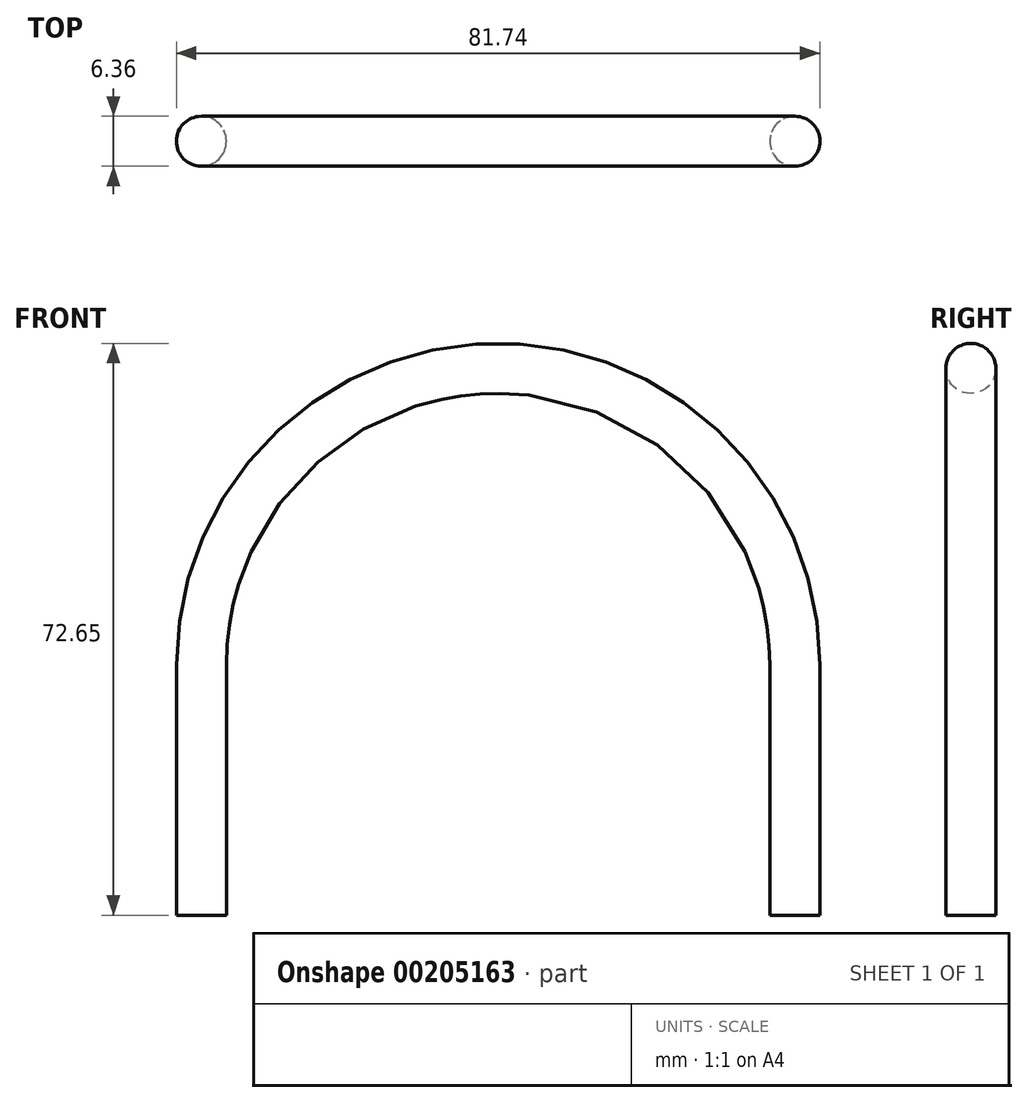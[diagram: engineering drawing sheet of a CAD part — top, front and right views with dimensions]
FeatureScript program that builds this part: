
annotation { "Feature Type Name" : "Feature", "Feature Type Description" : "" }
export const myFeature = defineFeature(function(context is Context, id is Id, definition is map)
    precondition{}
    {
        {
            var Q0;
            Q0=qCreatedBy(makeId("Front.planeOp"),FACE);
            var sketch = newSketch(context, id + "F0", { "sketchPlane" : qUnion([Q0])});
            skLineSegment(sketch, "E0", {"start": v(38.43, 0) * mm, "end": v(38.43, 31.78) * mm});
            skLineSegment(sketch, "E1", {"start": v(-36.96, 0) * mm, "end": v(-36.96, 31.78) * mm});
            skArc(sketch, "E2", {"start": v(38.43, 31.78) * mm, "mid": v(0.74, 69.48) * mm, "end": v(-36.96, 31.78) * mm});
            skSolve(sketch);
        }
        {
            var Q0;
            Q0=qCreatedBy(makeId("Top.planeOp"),FACE);
            var sketch = newSketch(context, id + "F1", { "sketchPlane" : qUnion([Q0])});
            skCircle(sketch, "E3", {"center": v(38.43, 0) * mm, "radius": 3.17 * mm});
            skSolve(sketch);
        }
        {
            var Q0;
            Q0=makeQuery(id+"F1.imprint","IMPRINT",FACE,{"disambiguationData":[TD([[makeQuery(id+"F1.imprint","IMPRINT",EDGE,{"derivedFrom":sQuery(id+"F1.wireOp",EDGE,"E3")}),1.0]])]});
            var Q1;
            Q1=sQuery(id+"F0.wireOp",EDGE,"E0");
            var Q2;
            Q2=sQuery(id+"F0.wireOp",EDGE,"E2");
            var Q3;
            Q3=sQuery(id+"F0.wireOp",EDGE,"E1");
            sweep(context, id + "F2", {"profiles" : qUnion([Q0]), "path" : qUnion([Q1, Q2, Q3])});
        }
    });
